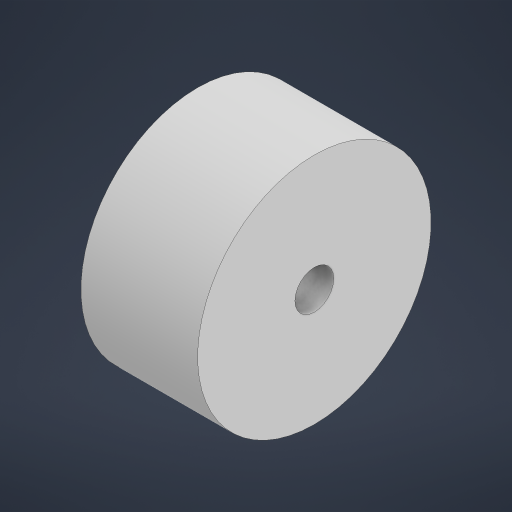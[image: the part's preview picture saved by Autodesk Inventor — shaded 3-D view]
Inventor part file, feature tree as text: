
AUTODESK INVENTOR PART (.ipt)
format: ipt  version: 2024 (Build 280153000, 153)  size: 161,280 bytes
history: native  units: mm
features: other x1, extrude x1, sketch x1
ambient origin geometry x8: Origin, YZ Plane, XZ Plane, XY Plane, X Axis, Y Axis, Z Axis, Center Point
bodies: Body1 (feature_tree)
feature tree (3):
  other  "솔리드1"
  extrude  "돌출1"  Depth=5.0mm
  sketch  "스케치1"
